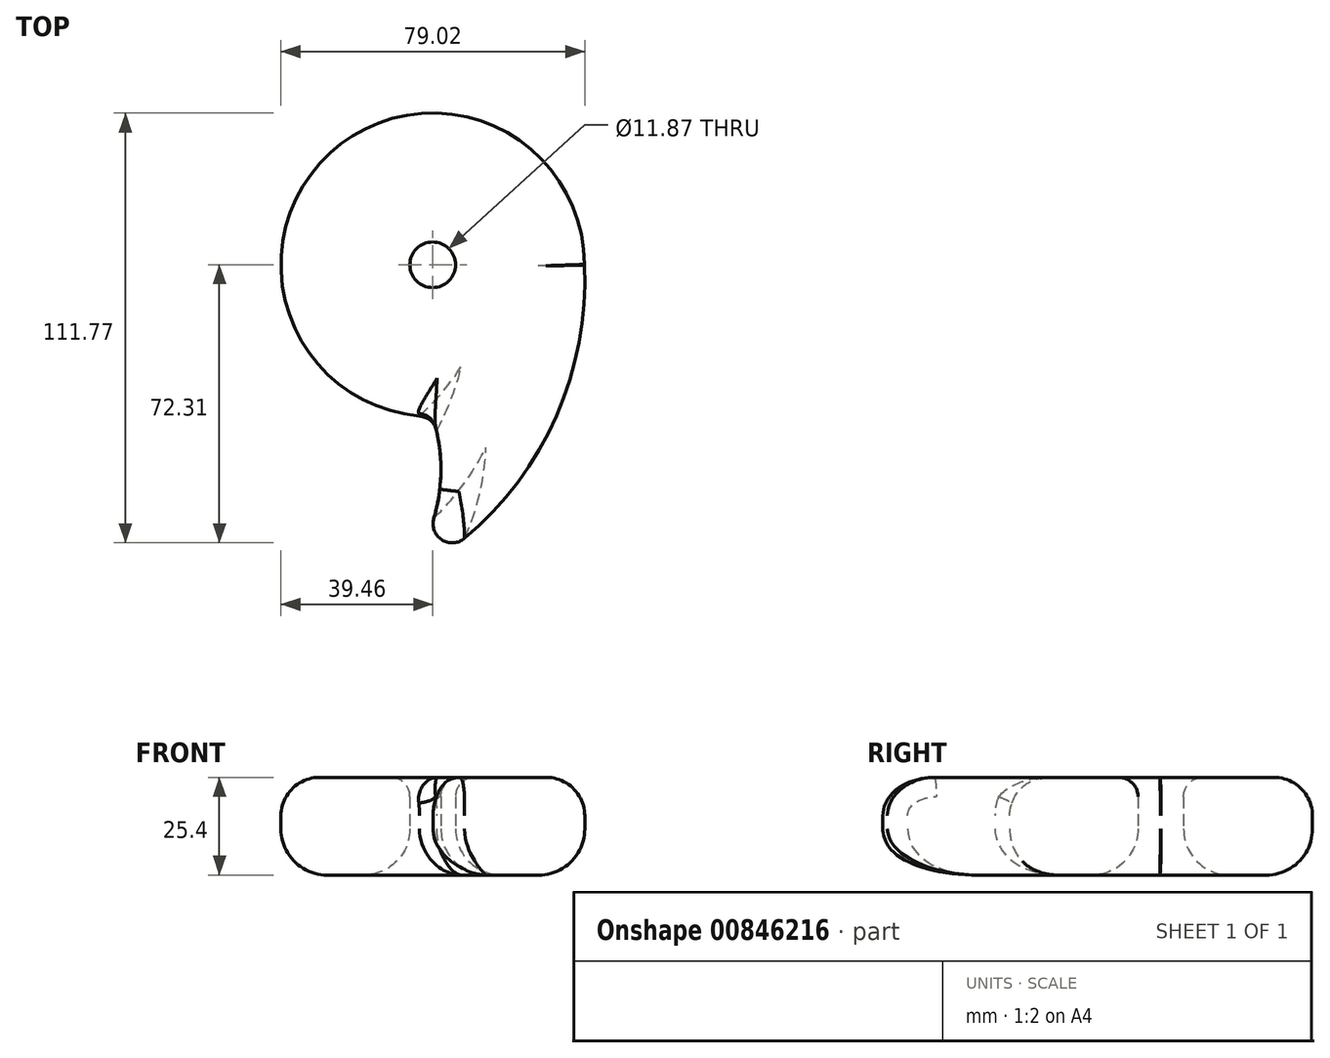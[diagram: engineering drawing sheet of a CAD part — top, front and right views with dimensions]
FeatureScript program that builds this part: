
annotation { "Feature Type Name" : "Feature", "Feature Type Description" : "" }
export const myFeature = defineFeature(function(context is Context, id is Id, definition is map)
    precondition{}
    {
        {
            var Q0;
            Q0=qCreatedBy(makeId("Top.planeOp"),FACE);
            var sketch = newSketch(context, id + "F0", { "sketchPlane" : qUnion([Q0])});
            skArc(sketch, "E0", {"start": v(39.46, 0) * mm, "mid": v(-27.9, 27.9) * mm, "end": v(0, -39.46) * mm});
            skPoint(sketch, "E1.orphan", {"position": v(0, -74.06) * mm});
            skArc(sketch, "E2", {"start": v(-10.37, -84.19) * mm, "mid": v(1, -63.26) * mm, "end": v(0, -39.46) * mm});
            skArc(sketch, "E3", {"start": v(-8.63, -82.28) * mm, "mid": v(27.61, -48.27) * mm, "end": v(39.46, 0) * mm});
            skSolve(sketch);
        }
        {
            var Q0;
            Q0 = qSketchRegion(id + "F0", true);
            extrude(context, id + "F1", {"entities" : qUnion([Q0]), "depth" : 25.4 * mm, "offsetDistance" : 25.4 * mm});
        }
        {
            var Q0;
            Q0=qCreatedBy(makeId("Top.planeOp"),FACE);
            var sketch = newSketch(context, id + "F2", { "sketchPlane" : qUnion([Q0])});
            skCircle(sketch, "E4", {"center": v(0, 0) * mm, "radius": 5.93 * mm});
            skSolve(sketch);
        }
        {
            var Q0;
            Q0 = qSketchRegion(id + "F2", true);
            extrude(context, id + "F3", {"entities" : qUnion([Q0]), "operationType" : NewBodyOperationType.REMOVE, "depth" : 25.4 * mm, "offsetDistance" : 25.4 * mm});
        }
        {
            var Q0;
            Q0=makeQuery(id+"F1.opExtrude","CAP_EDGE",EDGE,{"disambiguationData":[OSD([sQuery(id+"F0.wireOp",EDGE,"E0")])],"isStart":false});
            fillet(context, id + "F4", {"entities" : qUnion([Q0]), "radius" : 10 * mm, "tangentPropagation" : true, "allowEdgeOverflow" : false});
        }
        {
            var Q0;
            Q0=makeQuery(id+"F1.opExtrude","CAP_EDGE",EDGE,{"disambiguationData":[OSD([sQuery(id+"F0.wireOp",EDGE,"E0")])],"isStart":true});
            var Q1;
            Q1=makeQuery(id+"F1.opExtrude","CAP_FACE",FACE,{"disambiguationData":[OSD([sQuery(id+"F0.wireOp",EDGE,"E0"),sQuery(id+"F0.wireOp",EDGE,"as12nCty-biBN-vUkV-nSWW-IR48pDjWyOX9"),sQuery(id+"F0.wireOp",EDGE,"zXuleAu7-XCux-T0nj-OaMs-DEMq9Rjcxfo8")])],"isStart":true});
            fillet(context, id + "F5", {"entities" : qUnion([Q0, Q1]), "radius" : 12 * mm, "tangentPropagation" : true, "allowEdgeOverflow" : false});
        }
        {
            var Q0;
            Q0=makeQuery(id+"F4.opFillet","BLEND_FACE",FACE,{"disambiguationData":[OSD([sQuery(id+"F0.wireOp",EDGE,"as12nCty-biBN-vUkV-nSWW-IR48pDjWyOX9")])]});
            var Q1;
            Q1=makeQuery(id+"F1.opExtrude","CAP_FACE",FACE,{"disambiguationData":[OSD([sQuery(id+"F0.wireOp",EDGE,"E0"),sQuery(id+"F0.wireOp",EDGE,"as12nCty-biBN-vUkV-nSWW-IR48pDjWyOX9"),sQuery(id+"F0.wireOp",EDGE,"zXuleAu7-XCux-T0nj-OaMs-DEMq9Rjcxfo8")])],"isStart":false});
            fillet(context, id + "F6", {"entities" : qUnion([Q0, Q1]), "radius" : 5 * mm, "tangentPropagation" : true, "allowEdgeOverflow" : false});
        }
        {
            var Q0;
            Q0=makeQuery(id+"F4.opFillet","BLEND_FACE",FACE,{"disambiguationData":[OSD([sQuery(id+"F0.wireOp",EDGE,"E0")])]});
            var Q1;
            Q1=makeQuery(id+"F5.opFillet","BLEND_FACE",FACE,{"disambiguationData":[OSD([sQuery(id+"F0.wireOp",EDGE,"E0")])]});
            var Q2;
            Q2=makeQuery(id+"F1.opExtrude","SWEPT_FACE",FACE,{"disambiguationData":[OSD([sQuery(id+"F0.wireOp",EDGE,"E2")])]});
            var Q3;
            Q3=makeQuery(id+"F5.opFillet","BLEND_FACE",FACE,{"disambiguationData":[OSD([sQuery(id+"F0.wireOp",EDGE,"E2")])]});
            var Q4;
            Q4=makeQuery(id+"F6.opFillet","BLEND_FACE",FACE,{"disambiguationData":[OSD([sQuery(id+"F0.wireOp",EDGE,"E2")])]});
            fillet(context, id + "F7", {"entities" : qUnion([Q0, Q1, Q2, Q3, Q4]), "radius" : 5 * mm, "tangentPropagation" : true, "allowEdgeOverflow" : false});
        }
    });
